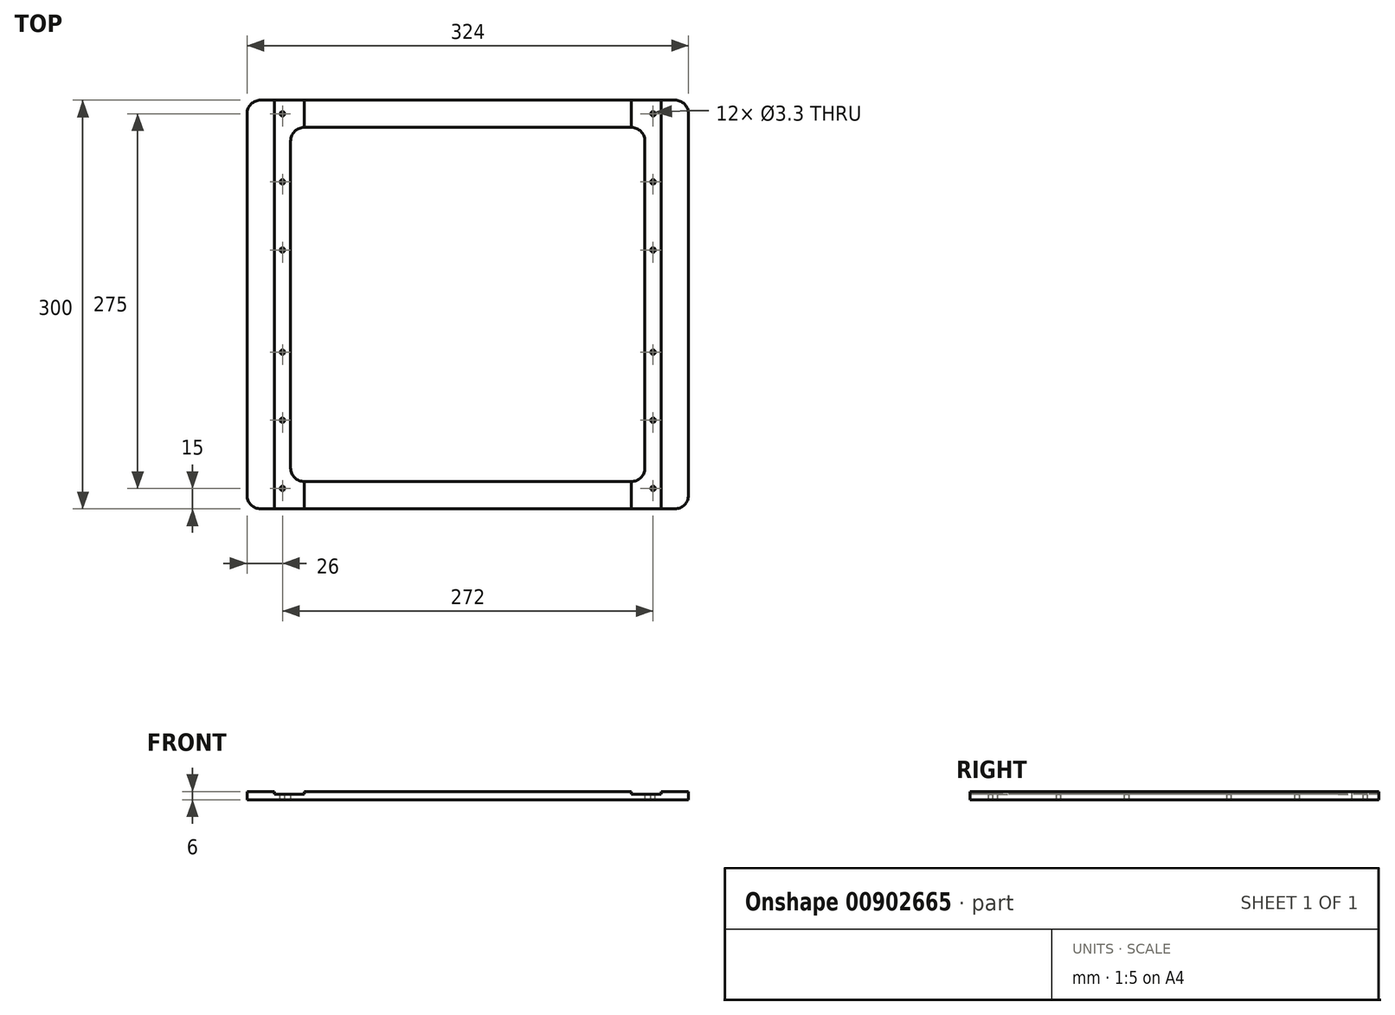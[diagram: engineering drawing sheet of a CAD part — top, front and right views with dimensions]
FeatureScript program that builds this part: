
annotation { "Feature Type Name" : "Feature", "Feature Type Description" : "" }
export const myFeature = defineFeature(function(context is Context, id is Id, definition is map)
    precondition{}
    {
        {
            var Q0;
            Q0=qCreatedBy(makeId("Top.planeOp"),FACE);
            var sketch = newSketch(context, id + "F0", { "sketchPlane" : qUnion([Q0])});
            skLineSegment(sketch, "E0.bottom", {"start": v(-130, 130) * mm, "end": v(130, 130) * mm});
            skLineSegment(sketch, "E0.top", {"start": v(-130, -130) * mm, "end": v(130, -130) * mm});
            skLineSegment(sketch, "E0.left", {"start": v(-130, 130) * mm, "end": v(-130, -130) * mm});
            skLineSegment(sketch, "E0.right", {"start": v(130, 130) * mm, "end": v(130, -130) * mm});
            skPoint(sketch, "E0.middle", {"position": v(0, 0) * mm});
            skLineSegment(sketch, "E1.bottom", {"start": v(-162, 150) * mm, "end": v(162, 150) * mm});
            skLineSegment(sketch, "E1.top", {"start": v(-162, -150) * mm, "end": v(162, -150) * mm});
            skLineSegment(sketch, "E1.left", {"start": v(-162, 150) * mm, "end": v(-162, -150) * mm});
            skLineSegment(sketch, "E1.right", {"start": v(162, 150) * mm, "end": v(162, -150) * mm});
            skLineSegment(sketch, "E2", {"start": v(-150, 0) * mm, "end": v(150, 0) * mm});
            skSolve(sketch);
        }
        {
            var Q0;
            Q0 = qSketchRegion(id + "F0", true);
            extrude(context, id + "F1", {"entities" : qUnion([Q0]), "depth" : 6 * mm, "offsetDistance" : 25 * mm});
        }
        {
            var Q0;
            Q0=makeQuery(id+"F1.opExtrude","SWEPT_EDGE",EDGE,{"disambiguationData":[OSD([sQuery(id+"F0.wireOp",EDGE,"E0.bottom"),sQuery(id+"F0.wireOp",EDGE,"E0.right")])]});
            var Q1;
            Q1=makeQuery(id+"F1.opExtrude","SWEPT_EDGE",EDGE,{"disambiguationData":[OSD([sQuery(id+"F0.wireOp",EDGE,"E0.bottom"),sQuery(id+"F0.wireOp",EDGE,"E0.left")])]});
            var Q2;
            Q2=makeQuery(id+"F1.opExtrude","SWEPT_EDGE",EDGE,{"disambiguationData":[OSD([sQuery(id+"F0.wireOp",EDGE,"E0.top"),sQuery(id+"F0.wireOp",EDGE,"E0.left")])]});
            var Q3;
            Q3=makeQuery(id+"F1.opExtrude","SWEPT_EDGE",EDGE,{"disambiguationData":[OSD([sQuery(id+"F0.wireOp",EDGE,"E0.top"),sQuery(id+"F0.wireOp",EDGE,"E0.right")])]});
            fillet(context, id + "F2", {"entities" : qUnion([Q0, Q1, Q2, Q3]), "radius" : 10 * mm, "tangentPropagation" : true, "allowEdgeOverflow" : false});
        }
        {
            var Q0;
            Q0=makeQuery(id+"F1.opExtrude","SWEPT_FACE",FACE,{"disambiguationData":[OSD([sQuery(id+"F0.wireOp",EDGE,"E1.top")])]});
            var sketch = newSketch(context, id + "F3", { "sketchPlane" : qUnion([Q0])});
            skLineSegment(sketch, "E3.bottom", {"start": v(-142, 6) * mm, "end": v(-120, 6) * mm});
            skLineSegment(sketch, "E3.top", {"start": v(-142, 4) * mm, "end": v(-120, 4) * mm});
            skLineSegment(sketch, "E3.left", {"start": v(-142, 6) * mm, "end": v(-142, 4) * mm});
            skLineSegment(sketch, "E3.right", {"start": v(-120, 6) * mm, "end": v(-120, 4) * mm});
            skLineSegment(sketch, "E4.bottom", {"start": v(142, 6) * mm, "end": v(120, 6) * mm});
            skLineSegment(sketch, "E4.top", {"start": v(142, 4) * mm, "end": v(120, 4) * mm});
            skLineSegment(sketch, "E4.left", {"start": v(142, 6) * mm, "end": v(142, 4) * mm});
            skLineSegment(sketch, "E4.right", {"start": v(120, 6) * mm, "end": v(120, 4) * mm});
            skSolve(sketch);
        }
        {
            var Q0;
            Q0 = qSketchRegion(id + "F3", true);
            extrude(context, id + "F4", {"entities" : qUnion([Q0]), "operationType" : NewBodyOperationType.REMOVE, "oppositeDirection" : true, "depth" : 300 * mm, "offsetDistance" : 25 * mm});
        }
        {
            var Q0;
            Q0=makeQuery(id+"F4.boolean.opBoolean","COPY",FACE,{"derivedFrom":makeQuery(id+"F4.opExtrude","SWEPT_FACE",FACE,{"disambiguationData":[OSD([sQuery(id+"F3.wireOp",EDGE,"E3.top")])]})});
            var sketch = newSketch(context, id + "F5", { "sketchPlane" : qUnion([Q0])});
            skPoint(sketch, "E5", {"position": v(-136, 140) * mm});
            skPoint(sketch, "E6", {"position": v(136, 140) * mm});
            skPoint(sketch, "E7.1.0.0", {"position": v(-136, 115) * mm});
            skPoint(sketch, "E7.1.0.1", {"position": v(136, 115) * mm});
            skPoint(sketch, "E7.2.0.0", {"position": v(-136, 90) * mm});
            skPoint(sketch, "E7.2.0.1", {"position": v(136, 90) * mm});
            skPoint(sketch, "E7.3.0.0", {"position": v(-136, 65) * mm});
            skPoint(sketch, "E7.3.0.1", {"position": v(136, 65) * mm});
            skPoint(sketch, "E7.4.0.0", {"position": v(-136, 40) * mm});
            skPoint(sketch, "E7.4.0.1", {"position": v(136, 40) * mm});
            skPoint(sketch, "E7.5.0.0", {"position": v(-136, 15) * mm});
            skPoint(sketch, "E7.5.0.1", {"position": v(136, 15) * mm});
            skPoint(sketch, "E7.6.0.0", {"position": v(-136, -10) * mm});
            skPoint(sketch, "E7.6.0.1", {"position": v(136, -10) * mm});
            skPoint(sketch, "E7.7.0.0", {"position": v(-136, -35) * mm});
            skPoint(sketch, "E7.7.0.1", {"position": v(136, -35) * mm});
            skPoint(sketch, "E7.8.0.0", {"position": v(-136, -60) * mm});
            skPoint(sketch, "E7.8.0.1", {"position": v(136, -60) * mm});
            skPoint(sketch, "E7.9.0.0", {"position": v(-136, -85) * mm});
            skPoint(sketch, "E7.9.0.1", {"position": v(136, -85) * mm});
            skPoint(sketch, "E7.10.0.0", {"position": v(-136, -110) * mm});
            skPoint(sketch, "E7.10.0.1", {"position": v(136, -110) * mm});
            skPoint(sketch, "E7.11.0.0", {"position": v(-136, -135) * mm});
            skPoint(sketch, "E7.11.0.1", {"position": v(136, -135) * mm});
            skLineSegment(sketch, "E7.direction1", {"start": v(-136, 140) * mm, "end": v(-136, 115) * mm, "construction": true});
            skSolve(sketch);
        }
        {
            var Q0;
            Q0=sQuery(id+"F5.wireOp",VERTEX,"E5");
            var Q1;
            Q1=sQuery(id+"F5.wireOp",VERTEX,"E7.2.0.0");
            var Q2;
            Q2=sQuery(id+"F5.wireOp",VERTEX,"E7.11.0.0");
            var Q3;
            Q3=sQuery(id+"F5.wireOp",VERTEX,"E7.11.0.1");
            var Q4;
            Q4=sQuery(id+"F5.wireOp",VERTEX,"E7.2.0.1");
            var Q5;
            Q5=sQuery(id+"F5.wireOp",VERTEX,"E6");
            var Q6;
            Q6=sQuery(id+"F5.wireOp",VERTEX,"E7.9.0.1");
            var Q7;
            Q7=sQuery(id+"F5.wireOp",VERTEX,"E7.9.0.0");
            var Q8;
            Q8=sQuery(id+"F5.wireOp",VERTEX,"E7.4.0.0");
            var Q9;
            Q9=sQuery(id+"F5.wireOp",VERTEX,"E7.7.0.0");
            var Q10;
            Q10=sQuery(id+"F5.wireOp",VERTEX,"E7.7.0.1");
            var Q11;
            Q11=sQuery(id+"F5.wireOp",VERTEX,"E7.4.0.1");
            var Q12;
            Q12=makeQuery(id+"F1.opExtrude","SWEPT_BODY",BODY,{"disambiguationData":[OSD([sQuery(id+"F0.wireOp",EDGE,"E0.bottom"),sQuery(id+"F0.wireOp",EDGE,"E0.top"),sQuery(id+"F0.wireOp",EDGE,"E0.left"),sQuery(id+"F0.wireOp",EDGE,"E0.right"),sQuery(id+"F0.wireOp",EDGE,"E1.bottom"),sQuery(id+"F0.wireOp",EDGE,"E1.top"),sQuery(id+"F0.wireOp",EDGE,"E1.left"),sQuery(id+"F0.wireOp",EDGE,"E1.right")])]});
            hole(context, id + "F6", {"style" : HoleStyle.SIMPLE, "endStyle" : HoleEndStyle.BLIND, "standardTappedOrClearance" : lookupTablePath({ "standard" : "ISO", "engagement" : "75%", "pitch" : "0.7 mm", "size" : "M4", "type" : "Tapped" }), "standardBlindInLast" : lookupTablePath({ "standard" : "ISO", "engagement" : "75%", "pitch" : "0.7 mm", "size" : "M4", "type" : "Tapped" }), "holeDiameter" : 3.3 * mm, "majorDiameter" : 4 * mm, "showTappedDepth" : true, "holeDepth" : 14.1 * mm, "isTappedThrough" : true, "tappedDepth" : 12 * mm, "tapClearance" : 3, "locations" : qUnion([Q0, Q1, Q2, Q3, Q4, Q5, Q6, Q7, Q8, Q9, Q10, Q11]), "scope" : qUnion([Q12])});
        }
        {
            var Q0;
            Q0=makeQuery(id+"F1.opExtrude","SWEPT_EDGE",EDGE,{"disambiguationData":[OSD([sQuery(id+"F0.wireOp",EDGE,"E1.top"),sQuery(id+"F0.wireOp",EDGE,"E1.right")])]});
            var Q1;
            Q1=makeQuery(id+"F1.opExtrude","SWEPT_EDGE",EDGE,{"disambiguationData":[OSD([sQuery(id+"F0.wireOp",EDGE,"E1.bottom"),sQuery(id+"F0.wireOp",EDGE,"E1.right")])]});
            var Q2;
            Q2=makeQuery(id+"F1.opExtrude","SWEPT_EDGE",EDGE,{"disambiguationData":[OSD([sQuery(id+"F0.wireOp",EDGE,"E1.top"),sQuery(id+"F0.wireOp",EDGE,"E1.left")])]});
            var Q3;
            Q3=makeQuery(id+"F1.opExtrude","SWEPT_EDGE",EDGE,{"disambiguationData":[OSD([sQuery(id+"F0.wireOp",EDGE,"E1.bottom"),sQuery(id+"F0.wireOp",EDGE,"E1.left")])]});
            fillet(context, id + "F7", {"entities" : qUnion([Q0, Q1, Q2, Q3]), "radius" : 10 * mm, "tangentPropagation" : true, "allowEdgeOverflow" : false});
        }
    });
